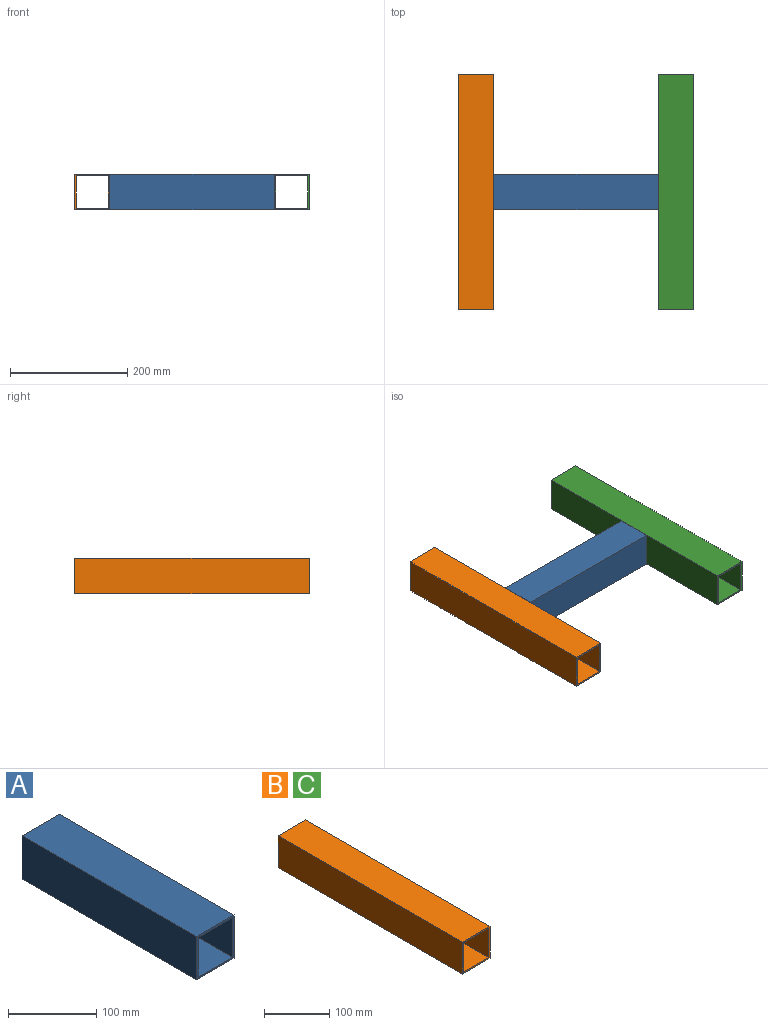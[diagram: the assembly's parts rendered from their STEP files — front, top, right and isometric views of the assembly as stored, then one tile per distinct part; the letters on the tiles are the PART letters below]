
ASSEMBLY  parts=3 mates=2
PART A: 10 faces, bbox 60x280x60 mm
  f0: plane 280x55mm, normal (1,0,0), area 15400mm2, adj f1,f7,f8,f9
  f1: plane 280x55mm, normal (0,0,-1), area 15400mm2, adj f0,f2,f8,f9
  f2: plane 280x55mm, normal (-1,0,0), area 15400mm2, adj f1,f7,f8,f9
  f3: plane 280x60mm, normal (0,0,1), area 16800mm2, adj f4,f6,f8,f9
  f4: plane 280x60mm, normal (-1,0,0), area 16800mm2, adj f3,f5,f8,f9
  f5: plane 280x60mm, normal (0,0,-1), area 16800mm2, adj f4,f6,f8,f9
  f6: plane 280x60mm, normal (1,0,0), area 16800mm2, adj f3,f5,f8,f9
  f7: plane 280x55mm, normal (0,0,1), area 15400mm2, adj f0,f2,f8,f9
  f8: plane 60x60mm, normal (0,-1,0), area 575mm2, adj f0,f1,f2,f3,f4,f5,f6,f7
  f9: plane 60x60mm, normal (0,1,0), area 575mm2, adj f0,f1,f2,f3,f4,f5,f6,f7
PART B: 10 faces, bbox 60x400x60 mm
  f0: plane 400x55mm, normal (1,0,0), area 22000mm2, adj f1,f7,f8,f9
  f1: plane 400x55mm, normal (0,0,-1), area 22000mm2, adj f0,f2,f8,f9
  f2: plane 400x55mm, normal (-1,0,0), area 22000mm2, adj f1,f7,f8,f9
  f3: plane 400x60mm, normal (0,0,1), area 24000mm2, adj f4,f6,f8,f9
  f4: plane 400x60mm, normal (-1,0,0), area 24000mm2, adj f3,f5,f8,f9
  f5: plane 400x60mm, normal (0,0,-1), area 24000mm2, adj f4,f6,f8,f9
  f6: plane 400x60mm, normal (1,0,0), area 24000mm2, adj f3,f5,f8,f9
  f7: plane 400x55mm, normal (0,0,1), area 22000mm2, adj f0,f2,f8,f9
  f8: plane 60x60mm, normal (0,-1,0), area 575mm2, adj f0,f1,f2,f3,f4,f5,f6,f7
  f9: plane 60x60mm, normal (0,1,0), area 575mm2, adj f0,f1,f2,f3,f4,f5,f6,f7
PART C: same geometry as B
PLACE A rot(axis=(-0.58,-0.58,-0.58),120deg) t=(13.66,-125.19,-43.34)mm
PLACE B t=(-296.34,74.81,-43.34)mm
PLACE C t=(43.66,74.81,-43.34)mm
MATE parallel B.f6 <-> A.f8  axis (1,0,0) through (-266.34,-125.19,-43.34)mm
MATE parallel C.f4 <-> A.f9  axis (-1,0,0) through (13.66,-125.19,-43.34)mm
